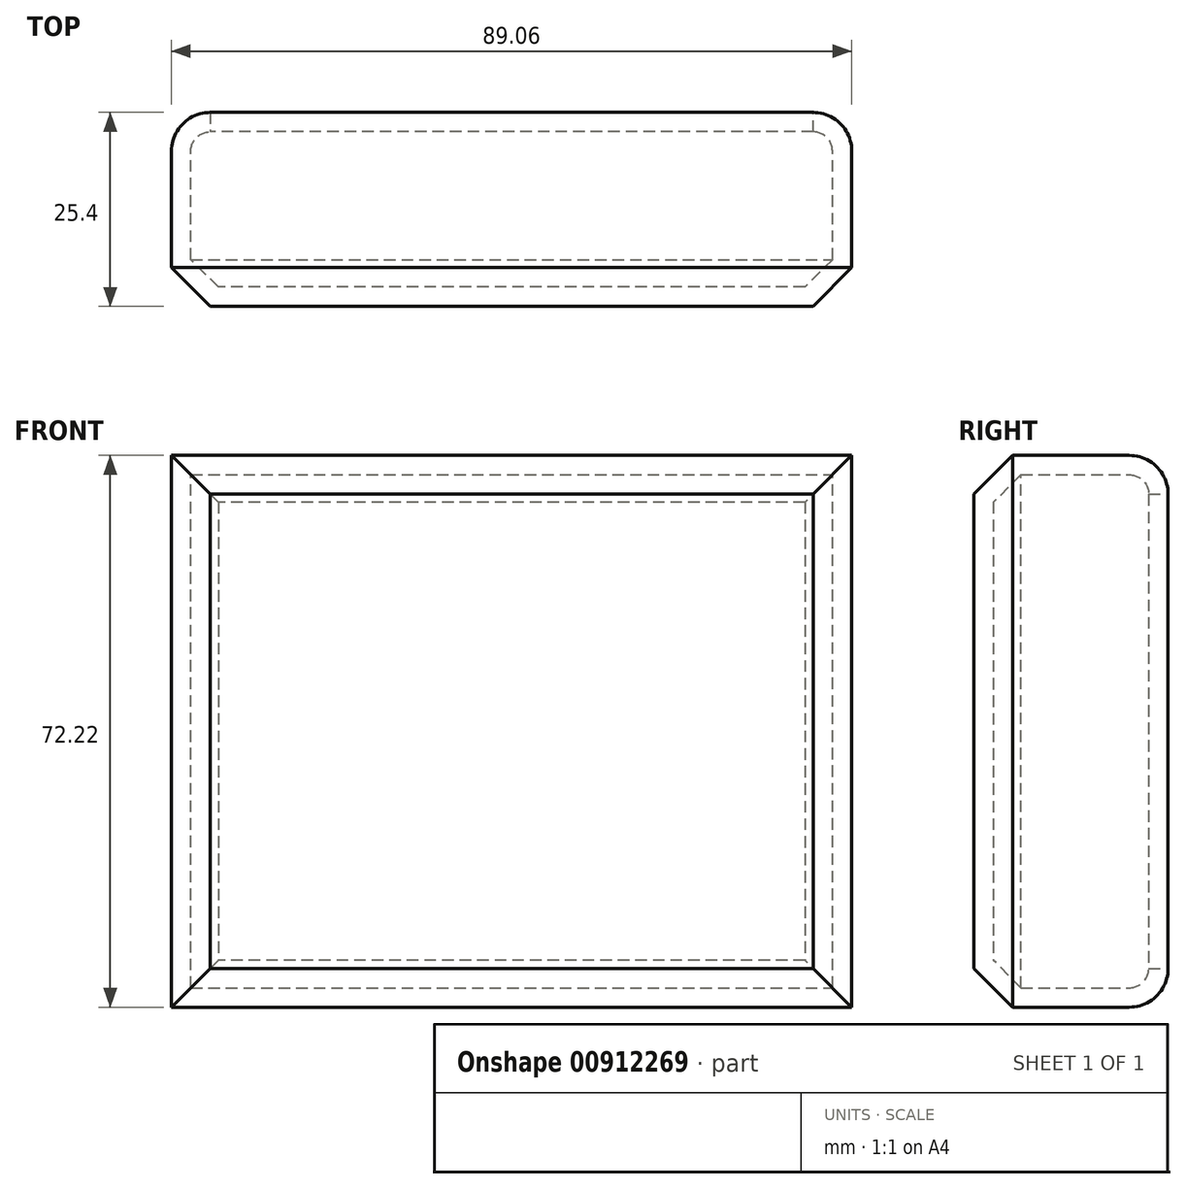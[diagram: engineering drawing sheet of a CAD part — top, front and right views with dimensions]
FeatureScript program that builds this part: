
annotation { "Feature Type Name" : "Feature", "Feature Type Description" : "" }
export const myFeature = defineFeature(function(context is Context, id is Id, definition is map)
    precondition{}
    {
        {
            var Q0;
            Q0=qCreatedBy(makeId("Front.planeOp"),FACE);
            var sketch = newSketch(context, id + "F0", { "sketchPlane" : qUnion([Q0])});
            skLineSegment(sketch, "E0.bottom", {"start": v(-8.42, 0) * mm, "end": v(-97.48, 0) * mm});
            skLineSegment(sketch, "E0.top", {"start": v(-8.42, -72.22) * mm, "end": v(-97.48, -72.22) * mm});
            skLineSegment(sketch, "E0.left", {"start": v(-8.42, 0) * mm, "end": v(-8.42, -72.22) * mm});
            skLineSegment(sketch, "E0.right", {"start": v(-97.48, 0) * mm, "end": v(-97.48, -72.22) * mm});
            skSolve(sketch);
        }
        {
            var Q0;
            Q0 = qSketchRegion(id + "F0", true);
            extrude(context, id + "F1", {"entities" : qUnion([Q0]), "depth" : 25.4 * mm, "offsetDistance" : 25.4 * mm});
        }
        {
            var Q0;
            Q0=makeQuery(id+"F1.opExtrude","CAP_EDGE",EDGE,{"disambiguationData":[OSD([sQuery(id+"F0.wireOp",EDGE,"E0.right")])],"isStart":false});
            var Q1;
            Q1=makeQuery(id+"F1.opExtrude","CAP_EDGE",EDGE,{"disambiguationData":[OSD([sQuery(id+"F0.wireOp",EDGE,"E0.bottom")])],"isStart":false});
            var Q2;
            Q2=makeQuery(id+"F1.opExtrude","CAP_EDGE",EDGE,{"disambiguationData":[OSD([sQuery(id+"F0.wireOp",EDGE,"E0.left")])],"isStart":false});
            var Q3;
            Q3=makeQuery(id+"F1.opExtrude","CAP_EDGE",EDGE,{"disambiguationData":[OSD([sQuery(id+"F0.wireOp",EDGE,"E0.top")])],"isStart":false});
            chamfer(context, id + "F2", {"entities" : qUnion([Q0, Q1, Q2, Q3]), "width" : 5.08 * mm, "tangentPropagation" : true});
        }
        {
            var Q0;
            Q0=makeQuery(id+"F1.opExtrude","CAP_FACE",FACE,{"disambiguationData":[OSD([sQuery(id+"F0.wireOp",EDGE,"E0.bottom"),sQuery(id+"F0.wireOp",EDGE,"E0.top"),sQuery(id+"F0.wireOp",EDGE,"E0.left"),sQuery(id+"F0.wireOp",EDGE,"E0.right")])],"isStart":true});
            fillet(context, id + "F3", {"entities" : qUnion([Q0]), "radius" : 5.08 * mm, "tangentPropagation" : true, "allowEdgeOverflow" : false});
        }
        {
            var Q0;
            Q0=makeQuery(id+"F1.opExtrude","CAP_FACE",FACE,{"disambiguationData":[OSD([sQuery(id+"F0.wireOp",EDGE,"E0.bottom"),sQuery(id+"F0.wireOp",EDGE,"E0.top"),sQuery(id+"F0.wireOp",EDGE,"E0.left"),sQuery(id+"F0.wireOp",EDGE,"E0.right")])],"isStart":true});
            shell(context, id + "F4", {"entities" : qUnion([Q0]), "thickness" : 2.54 * mm});
        }
    });
